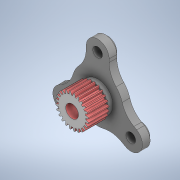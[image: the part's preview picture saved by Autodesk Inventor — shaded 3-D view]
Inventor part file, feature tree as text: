
AUTODESK INVENTOR PART (.ipt)
format: ipt  version: 2022 (Build 260153000, 153)  size: 419,840 bytes
history: mixed  units: mm
features: other x3, extrude x1, sketch x1, imported_body x1
ambient origin geometry x8: Origin, YZ Plane, XZ Plane, XY Plane, X Axis, Y Axis, Z Axis, Center Point
bodies: Solid1 (imported_parasolid)
feature tree (6):
  other  "Planet_Carrier_Modifed_with_sun_gear.iam"
  other  "Plamet_Carrier.ipt:1"
  other  "24_Teeth_Sun_Gear.ipt:1"
  extrude  "Extrusion1"  Depth=10.0mm TaperAngle=0.0deg
  sketch  "Sketch1"  dims[d0=10.0mm d1=7.0mm d2=0.0mm]
  imported_body  NMx_Import_Brep_tag  [imported B-rep: ~177 faces, bbox_mm=[31.788121, 26.496463, 14.0]]
